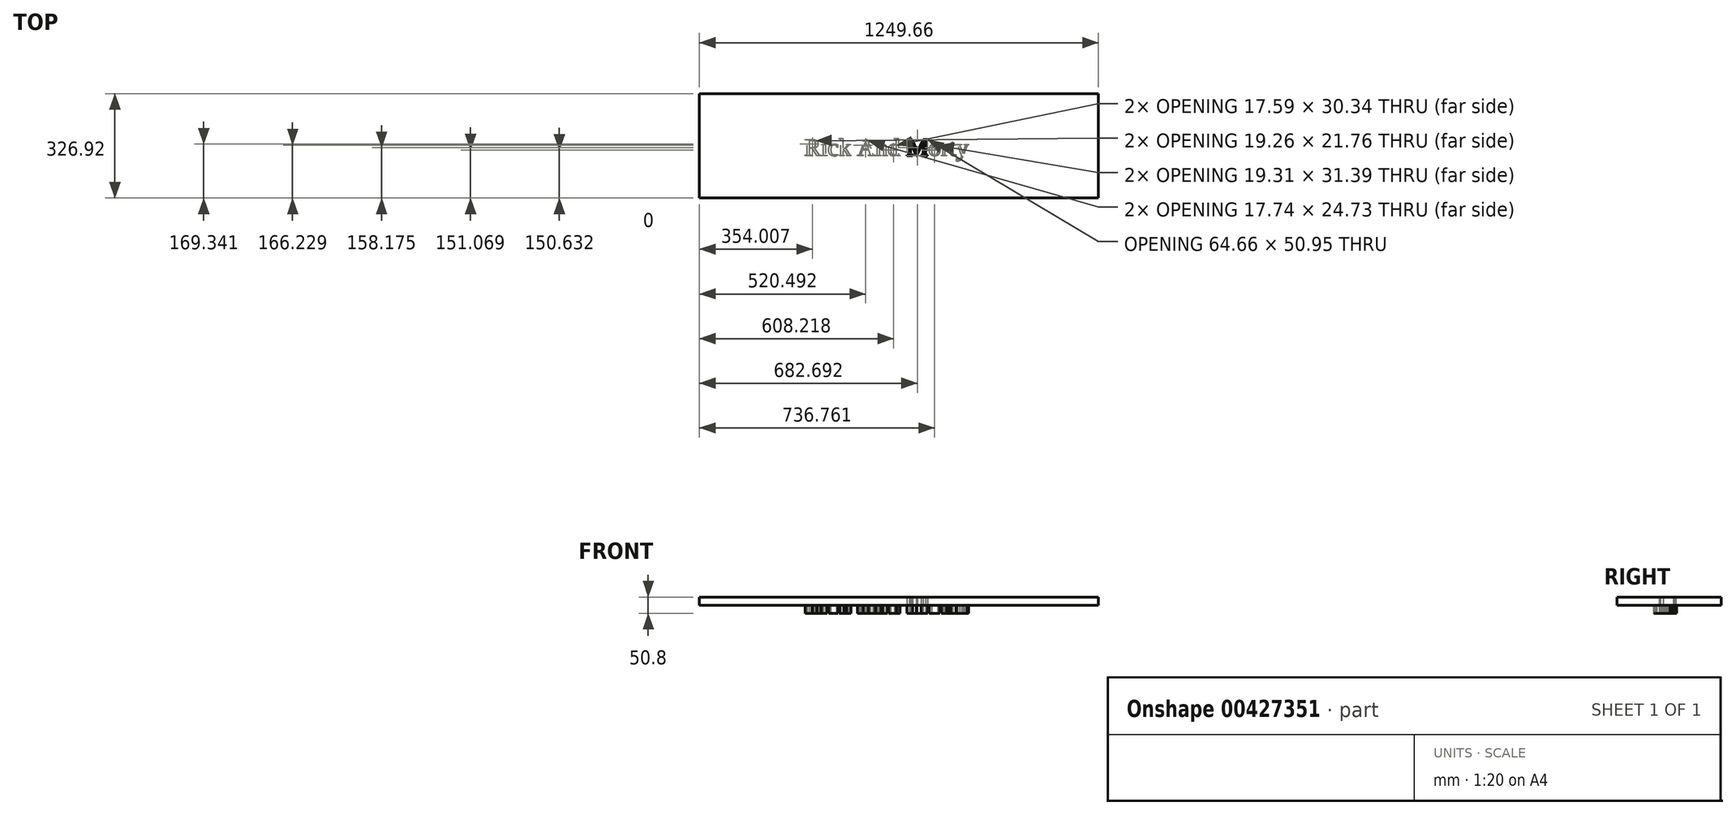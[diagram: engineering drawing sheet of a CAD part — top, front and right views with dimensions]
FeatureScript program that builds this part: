
annotation { "Feature Type Name" : "Feature", "Feature Type Description" : "" }
export const myFeature = defineFeature(function(context is Context, id is Id, definition is map)
    precondition{}
    {
        {
            var Q0;
            Q0=qCreatedBy(makeId("Top.planeOp"),FACE);
            var sketch = newSketch(context, id + "F0", { "sketchPlane" : qUnion([Q0])});
            skText(sketch, "E0", { "text": "Rick And Morty", "fontName": "Tinos-Regular.ttf"});
            const initialGuessF0  = {"E0": [-0.5189, 0, 1, 0, 0.05602]};
            skSetInitialGuess(sketch, initialGuessF0);
            skSolve(sketch);
        }
        {
            var Q0;
            Q0 = qSketchRegion(id + "F0", true);
            extrude(context, id + "F1", {"entities" : qUnion([Q0]), "depth" : 25.4 * mm});
        }
        {
            var Q0;
            Q0=makeQuery(id+"F1.opExtrude","CAP_FACE",FACE,{"disambiguationData":[OSD([sQuery(id+"F0.wireOp",EDGE,"E0.sketch_text.stroke-151"),sQuery(id+"F0.wireOp",EDGE,"E0.sketch_text.stroke-152"),sQuery(id+"F0.wireOp",EDGE,"E0.sketch_text.stroke-153"),sQuery(id+"F0.wireOp",EDGE,"E0.sketch_text.stroke-154"),sQuery(id+"F0.wireOp",EDGE,"E0.sketch_text.stroke-155"),sQuery(id+"F0.wireOp",EDGE,"E0.sketch_text.stroke-156"),sQuery(id+"F0.wireOp",EDGE,"E0.sketch_text.stroke-157"),sQuery(id+"F0.wireOp",EDGE,"E0.sketch_text.stroke-158"),sQuery(id+"F0.wireOp",EDGE,"E0.sketch_text.stroke-159"),sQuery(id+"F0.wireOp",EDGE,"E0.sketch_text.stroke-160"),sQuery(id+"F0.wireOp",EDGE,"E0.sketch_text.stroke-161"),sQuery(id+"F0.wireOp",EDGE,"E0.sketch_text.stroke-162"),sQuery(id+"F0.wireOp",EDGE,"E0.sketch_text.stroke-163"),sQuery(id+"F0.wireOp",EDGE,"E0.sketch_text.stroke-164"),sQuery(id+"F0.wireOp",EDGE,"E0.sketch_text.stroke-165"),sQuery(id+"F0.wireOp",EDGE,"E0.sketch_text.stroke-166"),sQuery(id+"F0.wireOp",EDGE,"E0.sketch_text.stroke-167"),sQuery(id+"F0.wireOp",EDGE,"E0.sketch_text.stroke-168"),sQuery(id+"F0.wireOp",EDGE,"E0.sketch_text.stroke-169"),sQuery(id+"F0.wireOp",EDGE,"E0.sketch_text.stroke-170"),sQuery(id+"F0.wireOp",EDGE,"E0.sketch_text.stroke-171"),sQuery(id+"F0.wireOp",EDGE,"E0.sketch_text.stroke-172"),sQuery(id+"F0.wireOp",EDGE,"E0.sketch_text.stroke-173"),sQuery(id+"F0.wireOp",EDGE,"E0.sketch_text.stroke-174"),sQuery(id+"F0.wireOp",EDGE,"E0.sketch_text.stroke-175")])],"isStart":false});
            var sketch = newSketch(context, id + "F2", { "sketchPlane" : qUnion([Q0])});
            skLineSegment(sketch, "E1.bottom", {"start": v(-847.17, 194.22) * mm, "end": v(402.49, 194.22) * mm});
            skLineSegment(sketch, "E1.top", {"start": v(-847.17, -132.7) * mm, "end": v(402.49, -132.7) * mm});
            skLineSegment(sketch, "E1.left", {"start": v(-847.17, 194.22) * mm, "end": v(-847.17, -132.7) * mm});
            skLineSegment(sketch, "E1.right", {"start": v(402.49, 194.22) * mm, "end": v(402.49, -132.7) * mm});
            skSolve(sketch);
        }
        {
            var Q0;
            Q0=makeQuery(id+"F2.imprint","IMPRINT",FACE,{"disambiguationData":[TD([[makeQuery(id+"F2.imprint","IMPRINT",EDGE,{"derivedFrom":sQuery(id+"F2.wireOp",EDGE,"E1.bottom")}),-1.0]])]});
            var Q1;
            Q1 = qSketchRegion(id + "F0", true);
            extrude(context, id + "F3", {"entities" : qUnion([Q0, Q1]), "depth" : 25.4 * mm});
        }
    });
